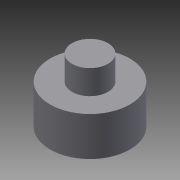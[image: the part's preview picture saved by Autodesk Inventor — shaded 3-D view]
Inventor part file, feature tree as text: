
AUTODESK INVENTOR PART (.ipt)
format: ipt  version: 2015 (Build 190159000, 159)  size: 89,600 bytes
history: native  units: mm
features: sketch x3, extrude x2, plane x1, hole x1
ambient origin geometry x8: Origin, YZ Plane, XZ Plane, XY Plane, X Axis, Y Axis, Z Axis, Center Point
bodies: Solid1 (feature_tree)
feature tree (7):
  extrude  "Extrusion1"  Depth=6.5mm TaperAngle=0.0deg
  plane  "Work Plane1"
  hole  "Hole1"  [1 undecoded]
  extrude  "Extrusion3"  Depth=4.049mm TaperAngle=0.0deg
  sketch  "Sketch1"  dims[d0=13.3mm d1=6.5mm d2=0.0mm]
  sketch  "Sketch3"  dims[d9=2.4mm]
  sketch  "Sketch4"  dims[d10=2.459mm d11=6.65mm d12=4.0mm d13=2.0mm d14=90.0deg d15=6.65mm d16=0.0mm d17=6.0mm d18=4.049mm d19=0.0mm]
note: 1 required parameter value undecoded (feature->parameter linkage not recoverable at this tier; creation-order binding heuristic only, values carry confidence <= 0.55)
